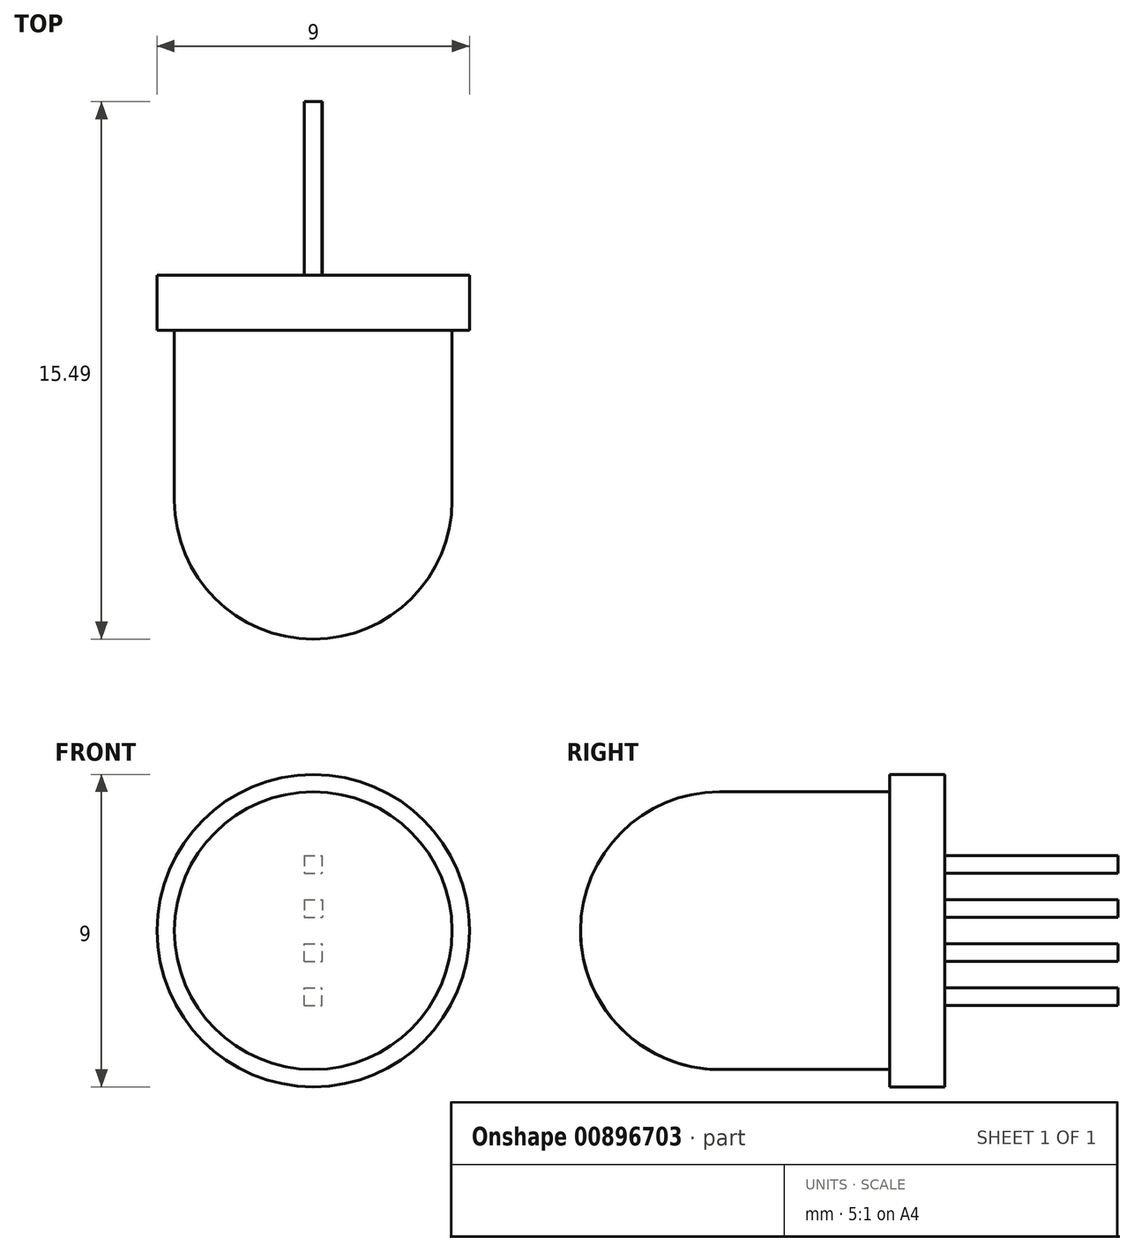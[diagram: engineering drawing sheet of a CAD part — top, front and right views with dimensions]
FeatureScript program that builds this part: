
annotation { "Feature Type Name" : "Feature", "Feature Type Description" : "" }
export const myFeature = defineFeature(function(context is Context, id is Id, definition is map)
    precondition{}
    {
        {
            var Q0;
            Q0=qCreatedBy(makeId("Front.planeOp"),FACE);
            var sketch = newSketch(context, id + "F0", { "sketchPlane" : qUnion([Q0])});
            skCircle(sketch, "E0", {"center": v(0, 0) * mm, "radius": 4 * mm});
            skCircle(sketch, "E1", {"center": v(0, 0) * mm, "radius": 4.5 * mm});
            skSolve(sketch);
        }
        {
            var Q0;
            Q0=makeQuery(id+"F0.imprint","IMPRINT",FACE,{"disambiguationData":[TD([[makeQuery(id+"F0.imprint","IMPRINT",EDGE,{"derivedFrom":sQuery(id+"F0.wireOp",EDGE,"E0")}),-1.0]])]});
            var Q1;
            Q1=makeQuery(id+"F0.imprint","IMPRINT",FACE,{"disambiguationData":[TD([[makeQuery(id+"F0.imprint","IMPRINT",EDGE,{"derivedFrom":sQuery(id+"F0.wireOp",EDGE,"E0")}),1.0]])]});
            extrude(context, id + "F1", {"entities" : qUnion([Q0, Q1]), "oppositeDirection" : true, "depth" : 1.59 * mm, "offsetDistance" : 25.4 * mm});
        }
        {
            var Q0;
            Q0=makeQuery(id+"F1.opExtrude","CAP_FACE",FACE,{"disambiguationData":[OSD([sQuery(id+"F0.wireOp",EDGE,"E1")])],"isStart":true});
            var sketch = newSketch(context, id + "F2", { "sketchPlane" : qUnion([Q0])});
            skCircle(sketch, "E2", {"center": v(0, 0) * mm, "radius": 4 * mm});
            skSolve(sketch);
        }
        {
            var Q0;
            Q0=makeQuery(id+"F2.imprint","IMPRINT",FACE,{"disambiguationData":[TD([[makeQuery(id+"F2.imprint","IMPRINT",EDGE,{"derivedFrom":sQuery(id+"F2.wireOp",EDGE,"E2")}),1.0]])]});
            extrude(context, id + "F3", {"entities" : qUnion([Q0]), "operationType" : NewBodyOperationType.ADD, "depth" : 8.9 * mm, "offsetDistance" : 25.4 * mm});
        }
        {
            var Q0;
            Q0=makeQuery(id+"F3.opExtrude","CAP_EDGE",EDGE,{"disambiguationData":[OSD([sQuery(id+"F2.wireOp",EDGE,"E2")])],"isStart":false});
            fillet(context, id + "F4", {"entities" : qUnion([Q0]), "radius" : 4 * mm, "tangentPropagation" : true, "allowEdgeOverflow" : false});
        }
        {
            var Q0;
            Q0=makeQuery(id+"F1.opExtrude","CAP_FACE",FACE,{"disambiguationData":[OSD([sQuery(id+"F0.wireOp",EDGE,"E1")])],"isStart":false});
            var sketch = newSketch(context, id + "F5", { "sketchPlane" : qUnion([Q0])});
            skLineSegment(sketch, "E3.bottom", {"start": v(0.25, 0.89) * mm, "end": v(-0.26, 0.89) * mm});
            skLineSegment(sketch, "E3.top", {"start": v(0.25, 0.38) * mm, "end": v(-0.26, 0.38) * mm});
            skLineSegment(sketch, "E3.left", {"start": v(0.25, 0.89) * mm, "end": v(0.25, 0.38) * mm});
            skLineSegment(sketch, "E3.right", {"start": v(-0.26, 0.89) * mm, "end": v(-0.26, 0.38) * mm});
            skPoint(sketch, "E3.middle", {"position": v(0, 0.64) * mm});
            skLineSegment(sketch, "E4.bottom", {"start": v(0.25, 2.16) * mm, "end": v(-0.25, 2.16) * mm});
            skLineSegment(sketch, "E4.top", {"start": v(0.25, 1.65) * mm, "end": v(-0.25, 1.65) * mm});
            skLineSegment(sketch, "E4.left", {"start": v(0.25, 2.16) * mm, "end": v(0.25, 1.65) * mm});
            skLineSegment(sketch, "E4.right", {"start": v(-0.25, 2.16) * mm, "end": v(-0.25, 1.65) * mm});
            skPoint(sketch, "E4.middle", {"position": v(0, 1.9) * mm});
            skLineSegment(sketch, "E5.MirrorCS", {"start": v(-0.26, -0.89) * mm, "end": v(-0.26, -0.38) * mm});
            skLineSegment(sketch, "E6.MirrorCS", {"start": v(-0.25, -2.16) * mm, "end": v(-0.25, -1.65) * mm});
            skLineSegment(sketch, "E7.MirrorCS", {"start": v(0.25, -0.38) * mm, "end": v(-0.26, -0.38) * mm});
            skLineSegment(sketch, "E8.MirrorCS", {"start": v(0.25, -1.65) * mm, "end": v(-0.25, -1.65) * mm});
            skLineSegment(sketch, "E9.MirrorCS", {"start": v(0.25, -2.16) * mm, "end": v(0.25, -1.65) * mm});
            skLineSegment(sketch, "E10.MirrorCS", {"start": v(0.25, -0.89) * mm, "end": v(-0.26, -0.89) * mm});
            skPoint(sketch, "E11.MirrorP", {"position": v(0, -1.9) * mm});
            skPoint(sketch, "E12.MirrorP", {"position": v(0, -0.64) * mm});
            skLineSegment(sketch, "E13.MirrorCS", {"start": v(0.25, -0.89) * mm, "end": v(0.25, -0.38) * mm});
            skLineSegment(sketch, "E14.MirrorCS", {"start": v(0.25, -2.16) * mm, "end": v(-0.25, -2.16) * mm});
            skSolve(sketch);
        }
        {
            var Q0;
            Q0=makeQuery(id+"F5.imprint","IMPRINT",FACE,{"disambiguationData":[TD([[makeQuery(id+"F5.imprint","IMPRINT",EDGE,{"derivedFrom":sQuery(id+"F5.wireOp",EDGE,"E4.bottom")}),1.0]])]});
            var Q1;
            Q1=makeQuery(id+"F5.imprint","IMPRINT",FACE,{"disambiguationData":[TD([[makeQuery(id+"F5.imprint","IMPRINT",EDGE,{"derivedFrom":sQuery(id+"F5.wireOp",EDGE,"E3.bottom")}),1.0]])]});
            var Q2;
            Q2=makeQuery(id+"F5.imprint","IMPRINT",FACE,{"disambiguationData":[TD([[makeQuery(id+"F5.imprint","IMPRINT",EDGE,{"derivedFrom":sQuery(id+"F5.wireOp",EDGE,"E5.MirrorCS")}),-1.0]])]});
            var Q3;
            Q3=makeQuery(id+"F5.imprint","IMPRINT",FACE,{"disambiguationData":[TD([[makeQuery(id+"F5.imprint","IMPRINT",EDGE,{"derivedFrom":sQuery(id+"F5.wireOp",EDGE,"E6.MirrorCS")}),-1.0]])]});
            extrude(context, id + "F6", {"entities" : qUnion([Q0, Q1, Q2, Q3]), "operationType" : NewBodyOperationType.ADD, "depth" : 5 * mm, "offsetDistance" : 25.4 * mm});
        }
    });
